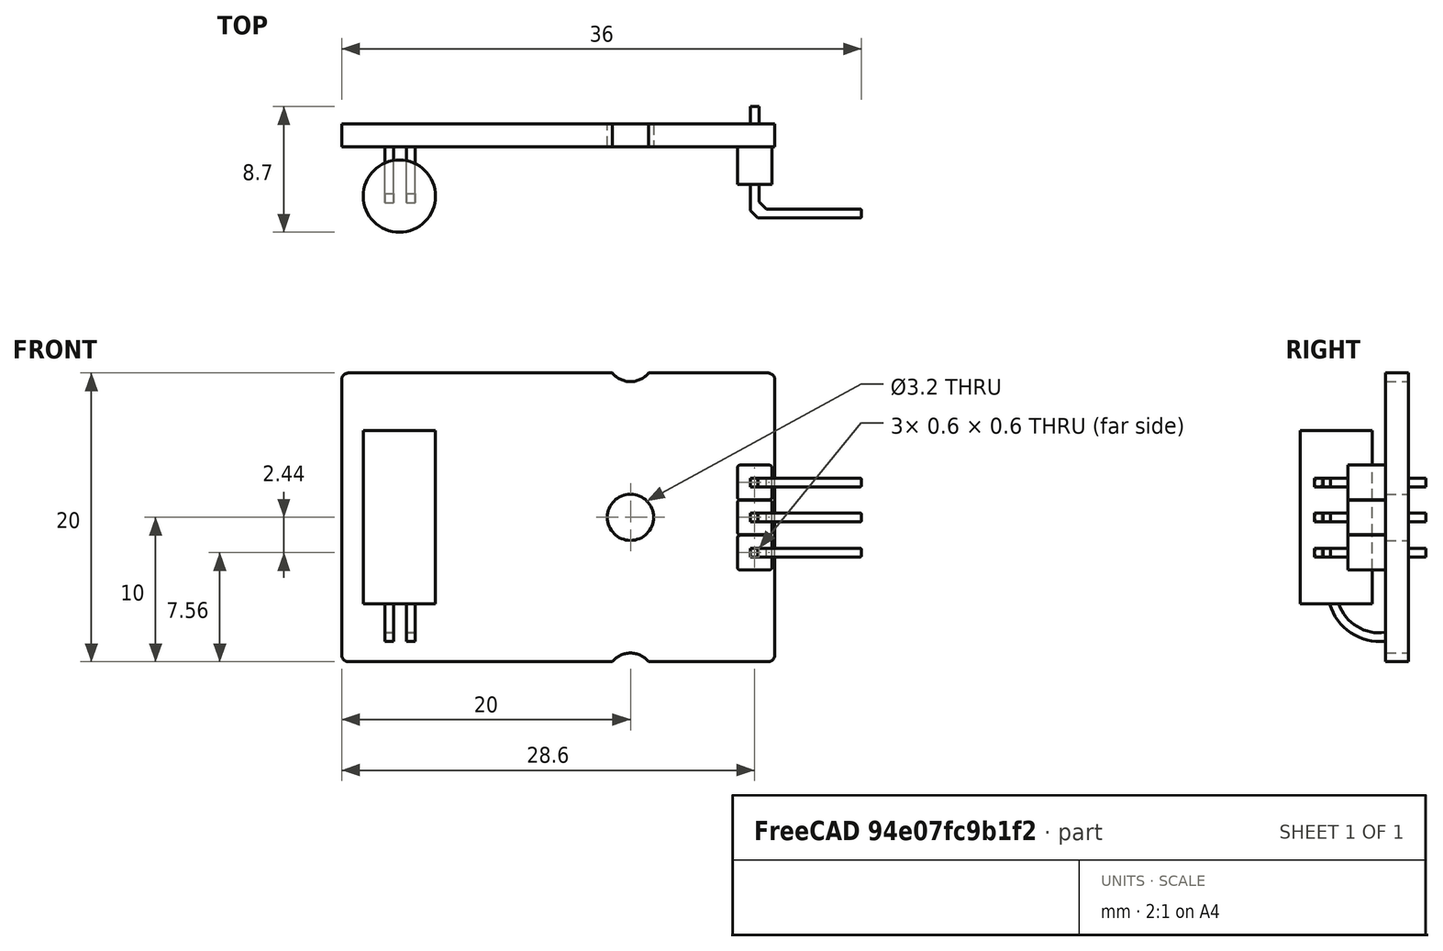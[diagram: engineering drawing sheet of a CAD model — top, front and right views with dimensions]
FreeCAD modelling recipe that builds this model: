
FCSTD DOCUMENT  (FreeCAD 0.20R29603 (Git))
Label: Sensor_Inclinacion
License: All rights reserved
LicenseURL: http://en.wikipedia.org/wiki/All_rights_reserved
objects: Part::Box×12, Part::MultiFuse×11, Part::Fillet×8, Part::Cylinder×6, Part::Chamfer×6, Part::Cut×5, Part::FeaturePython×2
note: 50 computed .brp shape members not serialized (recipe doc carries the construction recipe); baked Part::Feature solids carry a one-line shape summary decoded from their .brp

FEATURE [Part::Box] Box211  label="Cubo198"
  AttacherType = Attacher::AttachEngine3D
  Height = 1.6
  Length = 30
  Width = 20
FEATURE [Part::Box] Box212  label="Cubo199"
  AttacherType = Attacher::AttachEngine3D
  Height = 2.6
  Length = 2.4
  Placement = pos=(0,0,1.6) rot=(0,0,1;0rad)
  Width = 2.4
FEATURE [Part::Box] Box213  label="Cubo200"
  AttacherType = Attacher::AttachEngine3D
  Height = 7.7
  Length = 0.6
  Width = 0.6
FEATURE [Part::Box] Box214  label="Cubo201"
  AttacherType = Attacher::AttachEngine3D
  Height = 7.7
  Length = 0.6
  Placement = pos=(0,0,7.7) rot=(0,1,0;1.5708rad)
  Width = 0.6
FEATURE [Part::Box] Box215  label="Cubo202"
  AttacherType = Attacher::AttachEngine3D
  Height = 2.6
  Length = 2.4
  Placement = pos=(0,0,1.6) rot=(0,0,1;0rad)
  Width = 2.4
FEATURE [Part::Box] Box216  label="Cubo203"
  AttacherType = Attacher::AttachEngine3D
  Height = 7.7
  Length = 0.6
  Width = 0.6
FEATURE [Part::Box] Box217  label="Cubo204"
  AttacherType = Attacher::AttachEngine3D
  Height = 7.7
  Length = 0.6
  Placement = pos=(0,0,7.7) rot=(0,1,0;1.5708rad)
  Width = 0.6
FEATURE [Part::Box] Box218  label="Cubo205"
  AttacherType = Attacher::AttachEngine3D
  Height = 2.6
  Length = 2.4
  Placement = pos=(0,0,1.6) rot=(0,0,1;0rad)
  Width = 2.4
FEATURE [Part::Box] Box219  label="Cubo206"
  AttacherType = Attacher::AttachEngine3D
  Height = 7.7
  Length = 0.6
  Width = 0.6
FEATURE [Part::Box] Box220  label="Cubo207"
  AttacherType = Attacher::AttachEngine3D
  Height = 7.7
  Length = 0.6
  Placement = pos=(0,0,7.7) rot=(0,1,0;1.5708rad)
  Width = 0.6
FEATURE [Part::Box] Box221  label="Cubo208"
  AttacherType = Attacher::AttachEngine3D
  Height = 10
  Length = 10
  Placement = pos=(-14,-6,0) rot=(0,0,1;0rad)
  Width = 10
FEATURE [Part::Box] Box222  label="Cubo011"
  AttacherType = Attacher::AttachEngine3D
  Height = 10
  Length = 10
  Placement = pos=(-14,-11,-10) rot=(0,0,1;0rad)
  Width = 10
FEATURE [Part::Cylinder] Cylinder001  label="Cilindro001"
  Angle = 360
  AttacherType = Attacher::AttachEngine3D
  FirstAngle = 0
  Height = 10
  Placement = pos=(5,-11,0) rot=(0,0,1;0rad)
  Radius = 1.6
  SecondAngle = 0
FEATURE [Part::Cylinder] Cylinder190  label="Cilindro190"
  Angle = 360
  AttacherType = Attacher::AttachEngine3D
  FirstAngle = 0
  Height = 10
  Placement = pos=(5,0,0) rot=(0,0,1;0rad)
  Radius = 1.6
  SecondAngle = 0
FEATURE [Part::Cylinder] Cylinder191  label="Cilindro191"
  Angle = 360
  AttacherType = Attacher::AttachEngine3D
  FirstAngle = 0
  Height = 10
  Placement = pos=(5,11,0) rot=(0,0,1;0rad)
  Radius = 1.6
  SecondAngle = 0
FEATURE [Part::Cylinder] Cylinder192  label="Cilindro192"
  Angle = 360
  AttacherType = Attacher::AttachEngine3D
  FirstAngle = 0
  Height = 12
  Radius = 2.5
  SecondAngle = 0
FEATURE [Part::Cylinder] Cylinder193  label="Cilindro193"
  Angle = 360
  AttacherType = Attacher::AttachEngine3D
  FirstAngle = 0
  Height = 1
  Radius = 2
  SecondAngle = 0
FEATURE [Part::Cylinder] Cylinder194  label="Cilindro194"
  Angle = 360
  AttacherType = Attacher::AttachEngine3D
  FirstAngle = 0
  Height = 1
  Placement = pos=(0,0,11) rot=(0,0,1;0rad)
  Radius = 2
  SecondAngle = 0
FEATURE [Part::Fillet] Fillet161
  Base = -> Box211
  Edges = 3 edges r=0.5: [Edge1,Edge3,Edge7]
FEATURE [Part::Fillet] Fillet162
  Base = -> Fillet161
  Edges = 1 edges r=0.5: [Edge19]
  Placement = pos=(-15,-10,0) rot=(0,0,1;0rad)
FEATURE [Part::Cut] Cut259
  Base = -> Fillet162
  Tool = -> Cylinder190
FEATURE [Part::Cut] Cut260
  Base = -> Cut259
  Tool = -> Cylinder001
FEATURE [Part::Cut] Cut261  label="CircuitoImpreso"
  Base = -> Cut260
  Tool = -> Cylinder191
FEATURE [Part::Fillet] Fillet163  label="BasePlastico"
  Base = -> Box212
  Edges = 4 edges r=0.2: [Edge1,Edge3,Edge5,Edge7]
FEATURE [Part::Fillet] Fillet165  label="BasePlastico001"
  Base = -> Box215
  Edges = 4 edges r=0.2: [Edge1,Edge3,Edge5,Edge7]
FEATURE [Part::Fillet] Fillet167  label="BasePlastico002"
  Base = -> Box218
  Edges = 4 edges r=0.2: [Edge1,Edge3,Edge5,Edge7]
FEATURE [Part::MultiFuse] Fusion004
  Shapes = -> [Box219,Box220]
FEATURE [Part::Chamfer] Chamfer006
  Base = -> Fusion004
  Edges = 1 edges r=0.5: [Edge9]
FEATURE [Part::Chamfer] Chamfer007
  Base = -> Chamfer006
  Edges = 1 edges r=0.5: [Edge31]
FEATURE [Part::Fillet] Fillet168  label="CuerpoMetal002"
  Base = -> Chamfer007
  Edges = 4 edges r=0.1: [Edge5,Edge8,Edge14,Edge15]
  Placement = pos=(0.9,0.9,-1.2) rot=(0,0,1;0rad)
FEATURE [Part::MultiFuse] Fusion005  label="ConectorMacho002"
  Placement = pos=(12.4,-3.64,0) rot=(0,0,1;0rad)
  Shapes = -> [Fillet167,Fillet168]
FEATURE [Part::MultiFuse] Fusion006
  Shapes = -> [Cylinder192,Cylinder194]
FEATURE [Part::MultiFuse] Fusion007
  Placement = pos=(-11,6,5) rot=(1,0,0;1.5708rad)
  Shapes = -> [Fusion006,Cylinder193]
FEATURE [Part::MultiFuse] Fusion139
  Shapes = -> [Box213,Box214]
FEATURE [Part::Chamfer] Chamfer002
  Base = -> Fusion139
  Edges = 1 edges r=0.5: [Edge9]
FEATURE [Part::Chamfer] Chamfer003
  Base = -> Chamfer002
  Edges = 1 edges r=0.5: [Edge31]
FEATURE [Part::Fillet] Fillet164  label="CuerpoMetal"
  Base = -> Chamfer003
  Edges = 4 edges r=0.1: [Edge5,Edge8,Edge14,Edge15]
  Placement = pos=(0.9,0.9,-1.2) rot=(0,0,1;0rad)
FEATURE [Part::MultiFuse] Fusion001  label="ConectorMacho"
  Placement = pos=(12.4,-1.2,0) rot=(0,0,1;0rad)
  Shapes = -> [Fillet163,Fillet164]
FEATURE [Part::MultiFuse] Fusion140
  Shapes = -> [Box216,Box217]
FEATURE [Part::Chamfer] Chamfer004
  Base = -> Fusion140
  Edges = 1 edges r=0.5: [Edge9]
FEATURE [Part::Chamfer] Chamfer005
  Base = -> Chamfer004
  Edges = 1 edges r=0.5: [Edge31]
FEATURE [Part::Fillet] Fillet166  label="CuerpoMetal001"
  Base = -> Chamfer005
  Edges = 4 edges r=0.1: [Edge5,Edge8,Edge14,Edge15]
  Placement = pos=(0.9,0.9,-1.2) rot=(0,0,1;0rad)
FEATURE [Part::MultiFuse] Fusion003  label="ConectorMacho001"
  Placement = pos=(12.4,1.22,0) rot=(0,0,1;0rad)
  Shapes = -> [Fillet165,Fillet166]
FEATURE [Part::FeaturePython] Tube003  # WARN: FeaturePython — macro-defined, semantics opaque (R4)
  AttacherType = Attacher::AttachEngine3D
  Height = 0.6
  InnerRadius = 3
  OuterRadius = 3.6
  Placement = pos=(-12,-5,2) rot=(0,1,0;1.5708rad)
FEATURE [Part::FeaturePython] Tube004  # WARN: FeaturePython — macro-defined, semantics opaque (R4)
  AttacherType = Attacher::AttachEngine3D
  Height = 0.6
  InnerRadius = 3
  OuterRadius = 3.6
  Placement = pos=(-10.5,-5,2) rot=(0,1,0;1.5708rad)
FEATURE [Part::MultiFuse] Fusion008
  Shapes = -> [Tube004,Tube003]
FEATURE [Part::Cut] Cut262
  Base = -> Fusion008
  Tool = -> Box222
FEATURE [Part::Cut] Cut263  label="Sensor"
  Base = -> Cut262
  Tool = -> Box221
FEATURE [Part::MultiFuse] Fusion009
  Shapes = -> [Fusion007,Cut263]
FEATURE [Part::MultiFuse] Fusion010  label="Sensor_Inclinación"
  Placement = pos=(0,1,-0.6) rot=(1,0,0;1.5708rad)
  Shapes = -> [Cut261,Fusion001,Fusion003,Fusion005,Fusion009]
